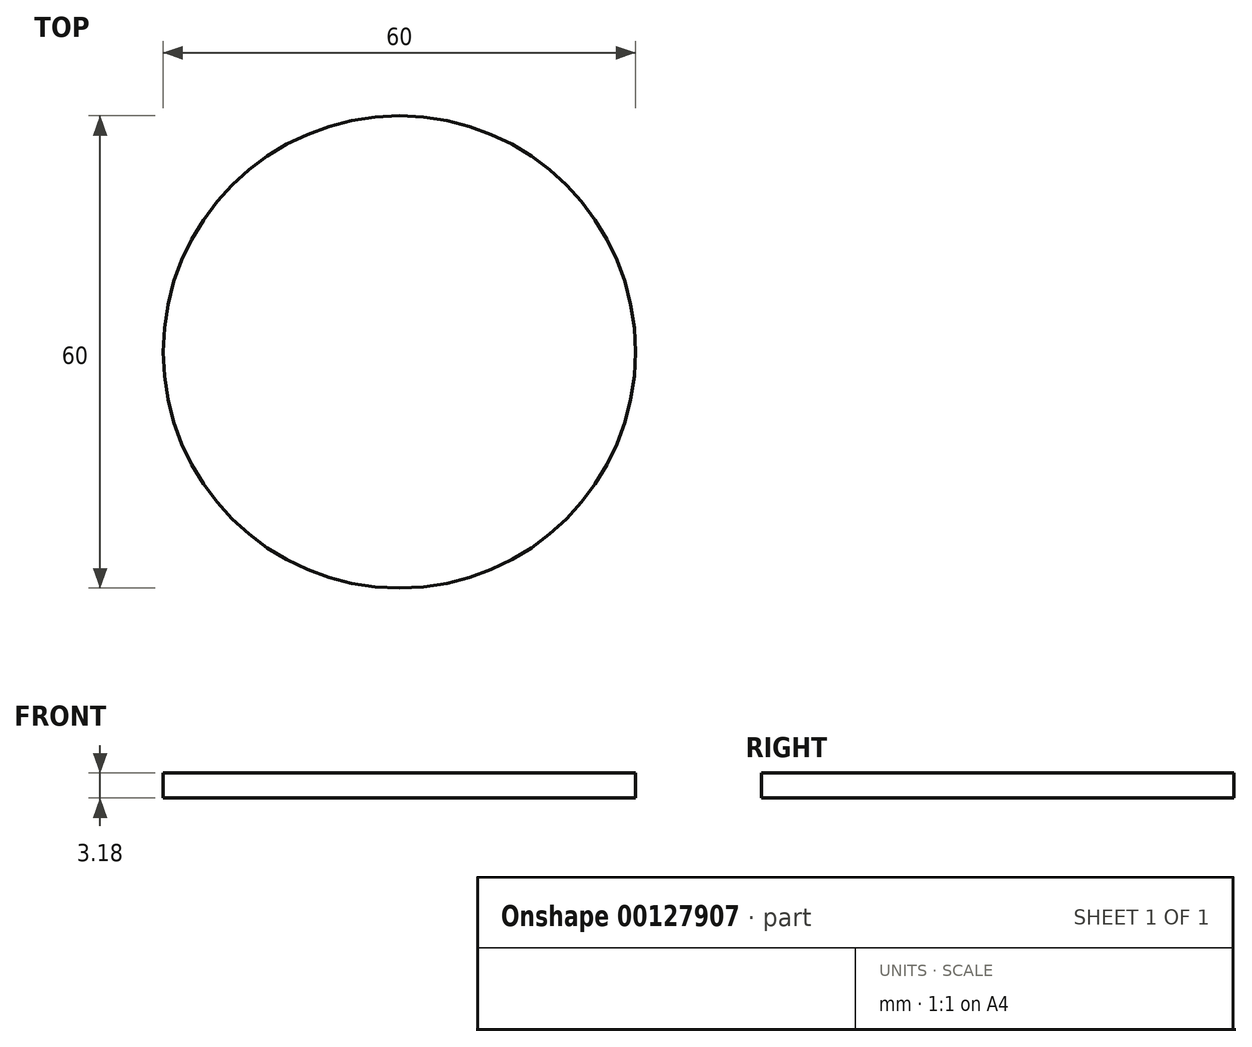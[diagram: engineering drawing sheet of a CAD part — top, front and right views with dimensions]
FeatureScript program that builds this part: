
annotation { "Feature Type Name" : "Feature", "Feature Type Description" : "" }
export const myFeature = defineFeature(function(context is Context, id is Id, definition is map)
    precondition{}
    {
        {
            var Q0;
            Q0=qCreatedBy(makeId("Top.planeOp"),FACE);
            var sketch = newSketch(context, id + "F0", { "sketchPlane" : qUnion([Q0])});
            skCircle(sketch, "E0", {"center": v(0, 0) * mm, "radius": 30 * mm});
            skSolve(sketch);
        }
        {
            var Q0;
            Q0=makeQuery(id+"F0.imprint","IMPRINT",FACE,{"disambiguationData":[TD([[makeQuery(id+"F0.imprint","IMPRINT",EDGE,{"derivedFrom":sQuery(id+"F0.wireOp",EDGE,"E0")}),1.0]])]});
            extrude(context, id + "F1", {"entities" : qUnion([Q0]), "depth" : 3.18 * mm});
        }
    });
